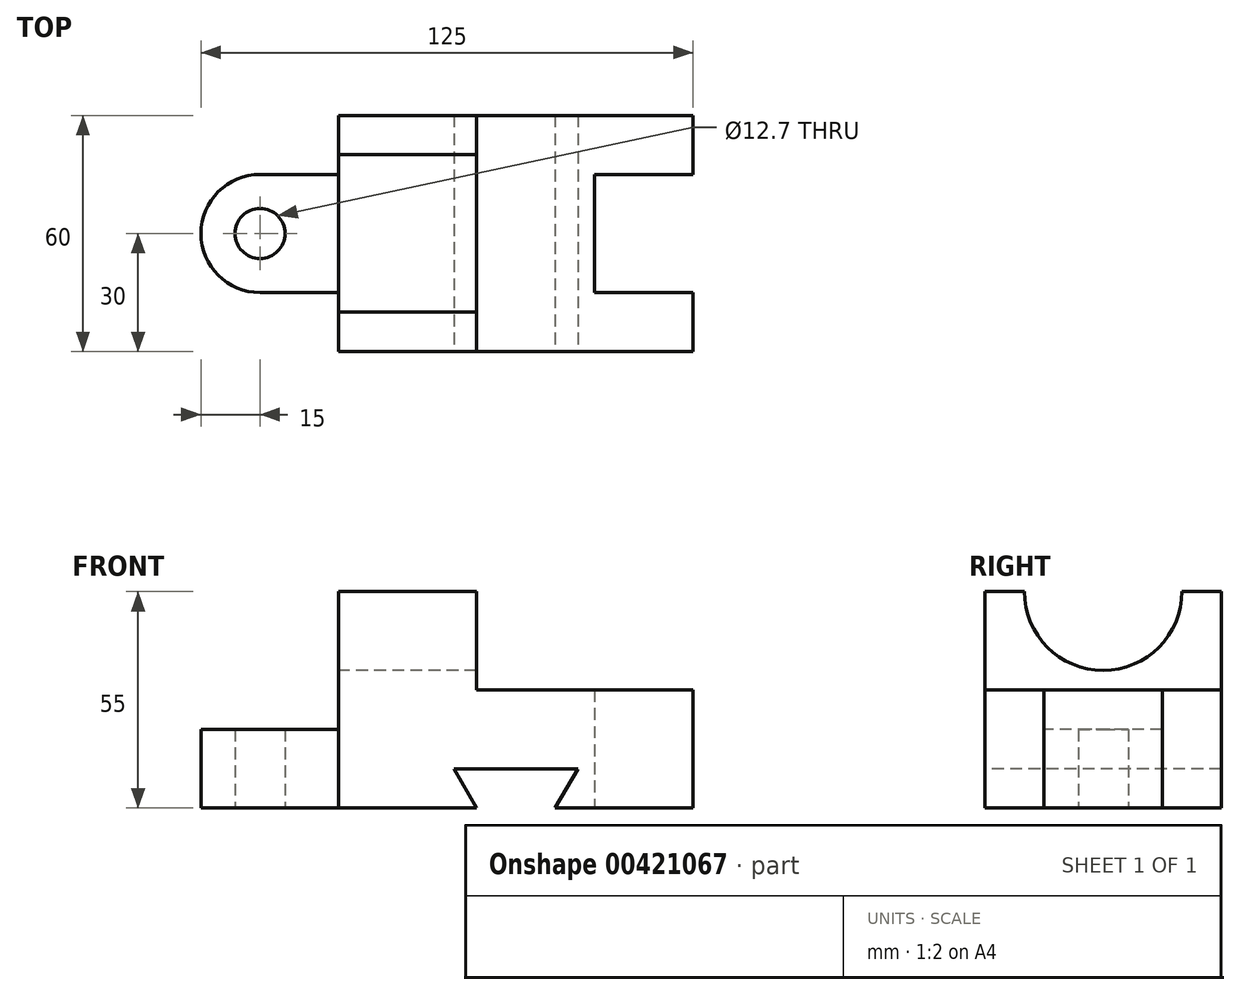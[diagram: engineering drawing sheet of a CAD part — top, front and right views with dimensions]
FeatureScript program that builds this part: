
annotation { "Feature Type Name" : "Feature", "Feature Type Description" : "" }
export const myFeature = defineFeature(function(context is Context, id is Id, definition is map)
    precondition{}
    {
        {
            var Q0;
            Q0=qCreatedBy(makeId("Top.planeOp"),FACE);
            var sketch = newSketch(context, id + "F0", { "sketchPlane" : qUnion([Q0])});
            skLineSegment(sketch, "E0.bottom", {"start": v(20, 30) * mm, "end": v(110, 30) * mm});
            skLineSegment(sketch, "E0.top", {"start": v(20, -30) * mm, "end": v(110, -30) * mm});
            skLineSegment(sketch, "E0.left", {"start": v(20, 30) * mm, "end": v(20, -30) * mm});
            skLineSegment(sketch, "E0.right", {"start": v(110, 30) * mm, "end": v(110, 15) * mm});
            skLineSegment(sketch, "E1.bottom", {"start": v(0, 15) * mm, "end": v(20, 15) * mm});
            skLineSegment(sketch, "E1.top", {"start": v(0, -15) * mm, "end": v(20, -15) * mm});
            skLineSegment(sketch, "E2", {"start": v(20, 0) * mm, "end": v(0, 0) * mm, "construction": true});
            skArc(sketch, "E3", {"start": v(0, 15) * mm, "mid": v(-15, 0) * mm, "end": v(0, -15) * mm});
            skCircle(sketch, "E4", {"center": v(0, 0) * mm, "radius": 6.35 * mm});
            skLineSegment(sketch, "E5.bottom", {"start": v(110, 15) * mm, "end": v(85, 15) * mm});
            skLineSegment(sketch, "E5.top", {"start": v(110, -15) * mm, "end": v(85, -15) * mm});
            skLineSegment(sketch, "E5.right", {"start": v(85, 15) * mm, "end": v(85, -15) * mm});
            skLineSegment(sketch, "E6", {"start": v(0, 0) * mm, "end": v(110, 0) * mm, "construction": true});
            skLineSegment(sketch, "E7.trimOffspring", {"start": v(110, -15) * mm, "end": v(110, -30) * mm});
            skLineSegment(sketch, "E8", {"start": v(55, 30) * mm, "end": v(55, -30) * mm});
            skSolve(sketch);
        }
        {
            var Q0;
            {var subQ1=sQuery(id+"F0.wireOp",EDGE,"E1.bottom");Q0=makeQuery(id+"F0.imprint","IMPRINT",FACE,{"disambiguationData":[TD([[makeQuery(id+"F0.imprint","IMPRINT",EDGE,{"derivedFrom":subQ1}),-1.0]])]});}
            extrude(context, id + "F1", {"entities" : qUnion([Q0]), "depth" : 20 * mm});
        }
        {
            var Q0;
            {var subQ0=sQuery(id+"F0.wireOp",EDGE,"E0.right");Q0=makeQuery(id+"F0.imprint","IMPRINT",FACE,{"disambiguationData":[TD([[makeQuery(id+"F0.imprint","IMPRINT",EDGE,{"derivedFrom":subQ0}),-1.0]])]});}
            var Q1;
            {var subQ6=sQuery(id+"F0.wireOp",EDGE,"E8");Q1=makeQuery(id+"F0.imprint","IMPRINT",FACE,{"disambiguationData":[TD([[makeQuery(id+"F0.imprint","IMPRINT",EDGE,{"derivedFrom":subQ6}),-1.0]])]});}
            extrude(context, id + "F2", {"entities" : qUnion([Q0, Q1]), "operationType" : NewBodyOperationType.ADD, "depth" : 30 * mm});
        }
        {
            var Q0;
            {var subQ6=sQuery(id+"F0.wireOp",EDGE,"E8");Q0=makeQuery(id+"F0.imprint","IMPRINT",FACE,{"disambiguationData":[TD([[makeQuery(id+"F0.imprint","IMPRINT",EDGE,{"derivedFrom":subQ6}),-1.0]])]});}
            extrude(context, id + "F3", {"entities" : qUnion([Q0]), "operationType" : NewBodyOperationType.ADD, "depth" : 55 * mm});
        }
        {
            var Q0;
            {var subQ0=sQuery(id+"F0.wireOp",EDGE,"E0.left");Q0=makeQuery(id+"F3.boolean.opBoolean","MERGE",FACE,{"derivedFrom":[makeQuery(id+"F2.opExtrude","SWEPT_FACE",FACE,{"disambiguationData":[OSD([subQ0])]}),makeQuery(id+"F3.opExtrude","SWEPT_FACE",FACE,{"disambiguationData":[OSD([subQ0])]})]});}
            var sketch = newSketch(context, id + "F4", { "sketchPlane" : qUnion([Q0])});
            skArc(sketch, "E9", {"start": v(-20, 55) * mm, "mid": v(0, 35) * mm, "end": v(20, 55) * mm});
            skLineSegment(sketch, "E10.0", {"start": v(-20, 55) * mm, "end": v(20, 55) * mm});
            skPoint(sketch, "E11.orphan", {"position": v(30, 55) * mm});
            skPoint(sketch, "E12.orphan", {"position": v(-30, 55) * mm});
            skSolve(sketch);
        }
        {
            var Q0;
            Q0=makeQuery(id+"F4.imprint","IMPRINT",FACE,{"disambiguationData":[TD([[makeQuery(id+"F4.imprint","IMPRINT",EDGE,{"derivedFrom":sQuery(id+"F4.wireOp",EDGE,"E9")}),1.0]])]});
            extrude(context, id + "F5", {"entities" : qUnion([Q0]), "operationType" : NewBodyOperationType.REMOVE, "endBound" : BoundingType.THROUGH_ALL, "oppositeDirection" : true, "depth" : 25 * mm});
        }
        {
            var Q0;
            {var subQ0=sQuery(id+"F0.wireOp",EDGE,"E0.top");Q0=makeQuery(id+"F3.boolean.opBoolean","MERGE",FACE,{"derivedFrom":[makeQuery(id+"F2.opExtrude","SWEPT_FACE",FACE,{"disambiguationData":[OSD([subQ0])]}),makeQuery(id+"F3.opExtrude","SWEPT_FACE",FACE,{"disambiguationData":[OSD([subQ0])]})]});}
            var sketch = newSketch(context, id + "F6", { "sketchPlane" : qUnion([Q0])});
            skLineSegment(sketch, "E13", {"start": v(55, 0) * mm, "end": v(49.23, 10) * mm});
            skLineSegment(sketch, "E14", {"start": v(49.23, 10) * mm, "end": v(80.77, 10) * mm});
            skLineSegment(sketch, "E15", {"start": v(80.77, 10) * mm, "end": v(75, 0) * mm});
            skLineSegment(sketch, "E16", {"start": v(55, 0) * mm, "end": v(75, 0) * mm});
            skSolve(sketch);
        }
        {
            var Q0;
            Q0=makeQuery(id+"F6.imprint","IMPRINT",FACE,{"disambiguationData":[TD([[makeQuery(id+"F6.imprint","IMPRINT",EDGE,{"derivedFrom":sQuery(id+"F6.wireOp",EDGE,"E13")}),-1.0]])]});
            extrude(context, id + "F7", {"entities" : qUnion([Q0]), "operationType" : NewBodyOperationType.REMOVE, "endBound" : BoundingType.THROUGH_ALL, "oppositeDirection" : true, "depth" : 25 * mm});
        }
    });
